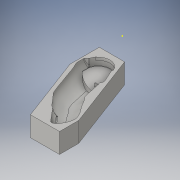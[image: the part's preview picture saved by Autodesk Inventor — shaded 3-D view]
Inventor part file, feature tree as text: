
AUTODESK INVENTOR PART (.ipt)
format: ipt  version: 2016 (Build 200138000, 138)  size: 2,957,824 bytes
history: native  units: in
note: dims shown in document units (in); Inventor stores cm internally (conversion verified against a paired STEP export)
features: sketch x5, extrude x4, other x3, projected_geometry x1
ambient origin geometry x8: Origin, YZ Plane, XZ Plane, XY Plane, X Axis, Y Axis, Z Axis, Center Point
bodies: Solid1 (feature_tree)
feature tree (13):
  other  "Finger Mold 2.iam"
  other  "Finger Mold.ipt:1"
  other  "Full Rubber Finger.ipt:1"
  extrude  "Extrusion1"  TaperAngle=0.0deg  [1 undecoded]
  extrude  "Extrusion2"  Depth=0.75in
  extrude  "Extrusion3"  Depth=0.87in
  extrude  "Extrusion4"  Depth=1.0in TaperAngle=0.0deg
  sketch  "Sketch74"
  sketch  "Sketch2"  dims[d0=0.3937in d1=0.0in d2=0.0in]
  projected_geometry  "Projected Loop1"
  sketch  "Sketch3"  dims[d3=1.0in d4=0.0in d5=0.75in]
  sketch  "Sketch4"  dims[d6=0.57in d8=0.87in]
  sketch  "Sketch5"  dims[d9=1.0in d10=0.0in d11=1.0in d12=0.0in]
note: 1 required parameter value undecoded (feature->parameter linkage not recoverable at this tier; creation-order binding heuristic only, values carry confidence <= 0.55)
